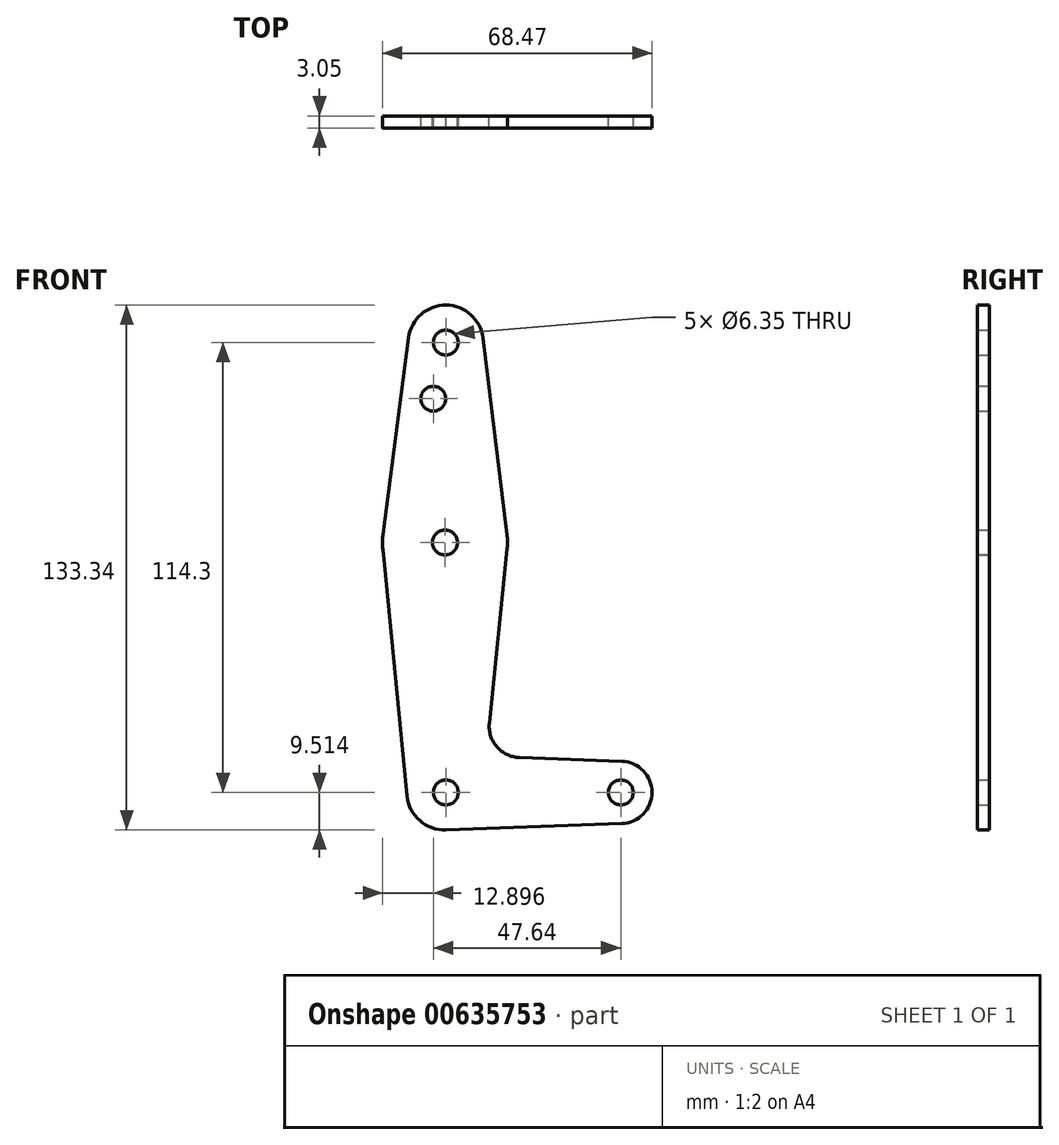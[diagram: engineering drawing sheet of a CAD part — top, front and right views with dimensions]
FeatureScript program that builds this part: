
annotation { "Feature Type Name" : "Feature", "Feature Type Description" : "" }
export const myFeature = defineFeature(function(context is Context, id is Id, definition is map)
    precondition{}
    {
        {
            var Q0;
            Q0=qCreatedBy(makeId("Front.planeOp"),FACE);
            var sketch = newSketch(context, id + "F0", { "sketchPlane" : qUnion([Q0])});
            skCircle(sketch, "E0", {"center": v(-58.93, 96.11) * mm, "radius": 9.53 * mm});
            skCircle(sketch, "E1", {"center": v(-59.13, 45.31) * mm, "radius": 15.88 * mm});
            skCircle(sketch, "E2", {"center": v(-59.25, -18.18) * mm, "radius": 9.53 * mm});
            skCircle(sketch, "E3", {"center": v(-14.46, -18.19) * mm, "radius": 7.94 * mm});
            skLineSegment(sketch, "E4", {"start": v(-58.91, -18.19) * mm, "end": v(-14.46, -18.19) * mm, "construction": true});
            skLineSegment(sketch, "E5", {"start": v(-58.93, 96.11) * mm, "end": v(-58.91, -18.19) * mm, "construction": true});
            skLineSegment(sketch, "E6", {"start": v(-68.38, 97.34) * mm, "end": v(-74.87, 47.36) * mm});
            skLineSegment(sketch, "E7", {"start": v(-49.48, 97.27) * mm, "end": v(-43.37, 47.24) * mm});
            skLineSegment(sketch, "E8", {"start": v(-40.25, -9.33) * mm, "end": v(-14.18, -10.25) * mm});
            skLineSegment(sketch, "E9", {"start": v(-58.92, -27.7) * mm, "end": v(-14.18, -26.12) * mm});
            skLineSegment(sketch, "E10", {"start": v(-74.7, 42.28) * mm, "end": v(-68.73, -19.1) * mm});
            skLineSegment(sketch, "E11", {"start": v(-47.87, -0.57) * mm, "end": v(-43.33, 43.7) * mm});
            skCircle(sketch, "E12", {"center": v(-62.1, 81.84) * mm, "radius": 3.18 * mm});
            skCircle(sketch, "E13", {"center": v(-59.13, 45.31) * mm, "radius": 3.18 * mm});
            skCircle(sketch, "E14", {"center": v(-58.93, 96.11) * mm, "radius": 3.18 * mm});
            skCircle(sketch, "E15", {"center": v(-58.91, -18.19) * mm, "radius": 3.18 * mm});
            skCircle(sketch, "E16", {"center": v(-14.46, -18.19) * mm, "radius": 3.18 * mm});
            skLineSegment(sketch, "E17", {"start": v(-62.1, 81.84) * mm, "end": v(-58.93, 81.84) * mm, "construction": true});
            skArc(sketch, "E18.filletArc", {"start": v(-47.87, -0.57) * mm, "mid": v(-45.96, -6.6) * mm, "end": v(-40.25, -9.33) * mm});
            skSolve(sketch);
        }
        {
            var Q0;
            Q0 = qSketchRegion(id + "F0", true);
            extrude(context, id + "F1", {"entities" : qUnion([Q0]), "depth" : 3.05 * mm, "offsetDistance" : 25.4 * mm});
        }
    });
